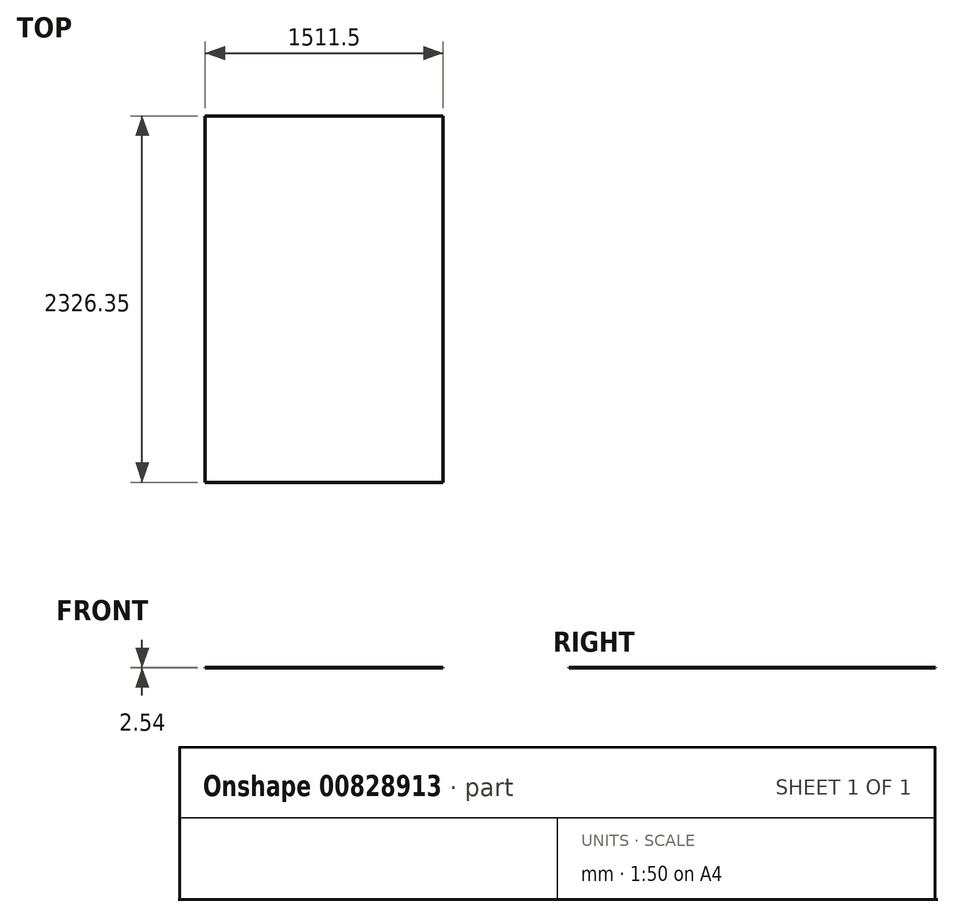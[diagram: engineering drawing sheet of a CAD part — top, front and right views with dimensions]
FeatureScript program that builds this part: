
annotation { "Feature Type Name" : "Feature", "Feature Type Description" : "" }
export const myFeature = defineFeature(function(context is Context, id is Id, definition is map)
    precondition{}
    {
        {
            var Q0;
            Q0=qCreatedBy(makeId("Top.planeOp"),FACE);
            var sketch = newSketch(context, id + "F0", { "sketchPlane" : qUnion([Q0])});
            skLineSegment(sketch, "E0.bottom", {"start": v(0, 0) * mm, "end": v(0, 0) * mm});
            skLineSegment(sketch, "E0.top", {"start": v(0, 0) * mm, "end": v(0, 0) * mm});
            skLineSegment(sketch, "E0.left", {"start": v(0, 0) * mm, "end": v(0, 0) * mm});
            skLineSegment(sketch, "E0.right", {"start": v(0, 0) * mm, "end": v(0, 0) * mm});
            skPoint(sketch, "E0.middle", {"position": v(0, 0) * mm});
            skLineSegment(sketch, "E1.bottom", {"start": v(597.94, -1634.67) * mm, "end": v(-913.56, -1634.67) * mm});
            skLineSegment(sketch, "E1.top", {"start": v(597.94, 691.68) * mm, "end": v(-913.56, 691.68) * mm});
            skLineSegment(sketch, "E1.left", {"start": v(597.94, -1634.67) * mm, "end": v(597.94, 691.68) * mm});
            skLineSegment(sketch, "E1.right", {"start": v(-913.56, -1634.67) * mm, "end": v(-913.56, 691.68) * mm});
            skPoint(sketch, "E1.middle", {"position": v(-157.81, -471.5) * mm});
            skSolve(sketch);
        }
        {
            var Q0;
            Q0 = qSketchRegion(id + "F0", true);
            extrude(context, id + "F1", {"entities" : qUnion([Q0]), "depth" : 2.54 * mm, "offsetDistance" : 25.4 * mm});
        }
    });
